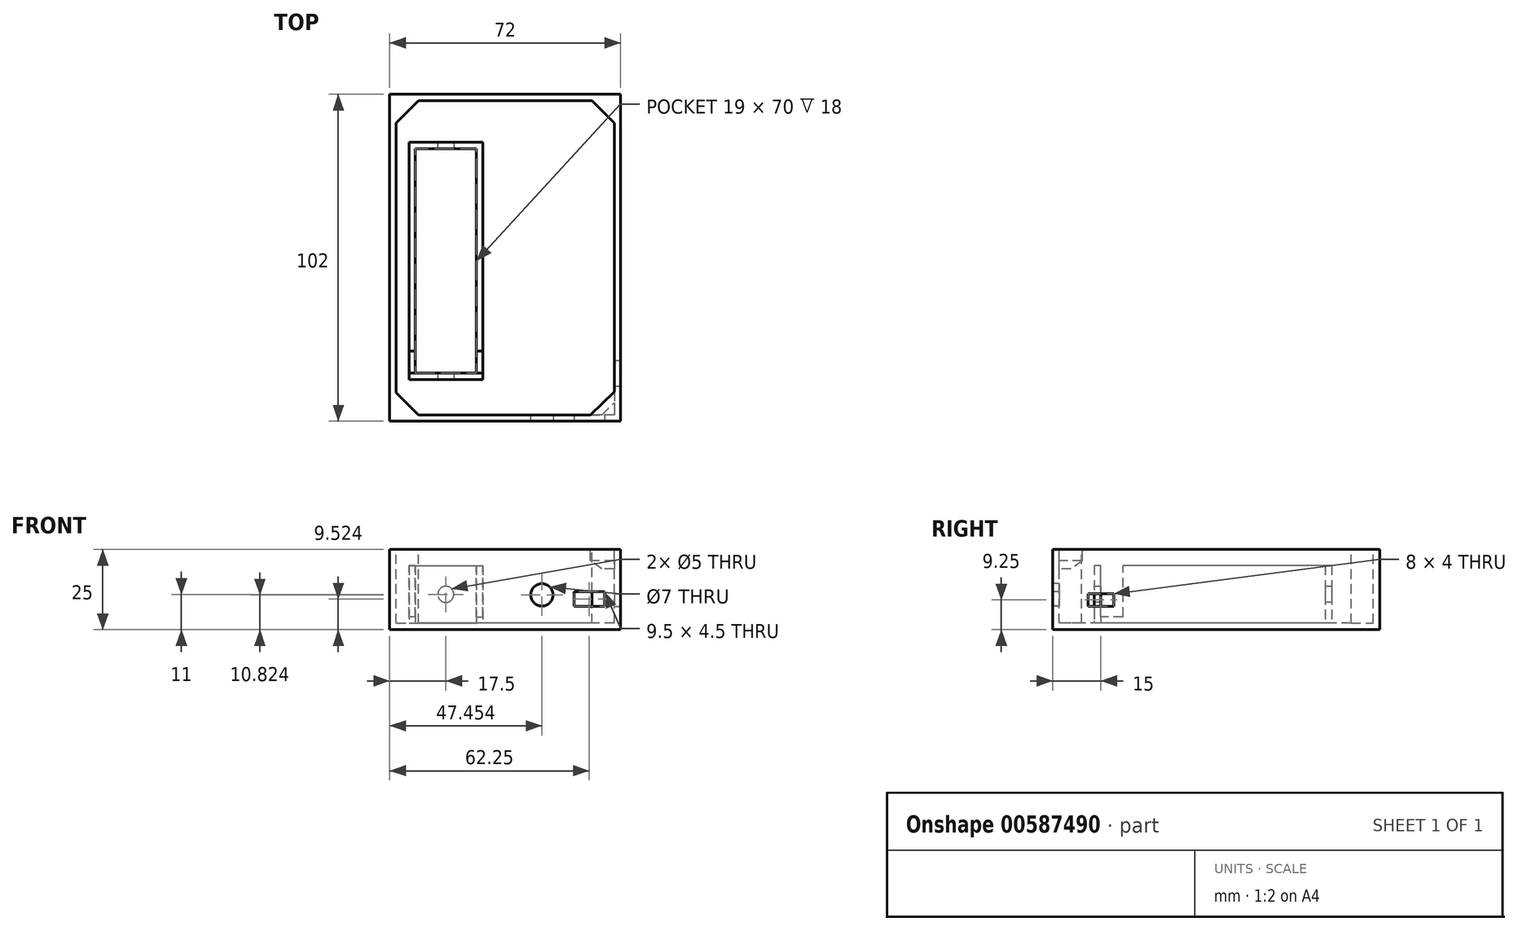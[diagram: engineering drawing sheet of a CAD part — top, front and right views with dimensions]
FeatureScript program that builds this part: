
annotation { "Feature Type Name" : "Feature", "Feature Type Description" : "" }
export const myFeature = defineFeature(function(context is Context, id is Id, definition is map)
    precondition{}
    {
        {
            var Q0;
            Q0=qCreatedBy(makeId("Top.planeOp"),FACE);
            var sketch = newSketch(context, id + "F0", { "sketchPlane" : qUnion([Q0])});
            skLineSegment(sketch, "E0.bottom", {"start": v(36, 51) * mm, "end": v(-36, 51) * mm});
            skLineSegment(sketch, "E0.top", {"start": v(36, -51) * mm, "end": v(-36, -51) * mm});
            skLineSegment(sketch, "E0.left", {"start": v(36, 51) * mm, "end": v(36, -51) * mm});
            skLineSegment(sketch, "E0.right", {"start": v(-36, 51) * mm, "end": v(-36, -51) * mm});
            skPoint(sketch, "E0.middle", {"position": v(0, 0) * mm});
            skSolve(sketch);
        }
        {
            var Q0;
            Q0 = qSketchRegion(id + "F0", true);
            extrude(context, id + "F1", {"entities" : qUnion([Q0]), "depth" : 25 * mm, "offsetDistance" : 25 * mm});
        }
        {
            var Q0;
            Q0=makeQuery(id+"F1.opExtrude","CAP_FACE",FACE,{"disambiguationData":[OSD([sQuery(id+"F0.wireOp",EDGE,"E0.bottom"),sQuery(id+"F0.wireOp",EDGE,"E0.top"),sQuery(id+"F0.wireOp",EDGE,"E0.left"),sQuery(id+"F0.wireOp",EDGE,"E0.right")])],"isStart":false});
            var sketch = newSketch(context, id + "F2", { "sketchPlane" : qUnion([Q0])});
            skLineSegment(sketch, "E1.bottom", {"start": v(27.06, 49) * mm, "end": v(-27.06, 49) * mm});
            skLineSegment(sketch, "E1.top", {"start": v(34, -49) * mm, "end": v(-27.06, -49) * mm});
            skLineSegment(sketch, "E1.left", {"start": v(34, 42.06) * mm, "end": v(34, -49) * mm});
            skLineSegment(sketch, "E1.right", {"start": v(-34, 42.06) * mm, "end": v(-34, -42.06) * mm});
            skPoint(sketch, "E1.middle", {"position": v(0, 0) * mm});
            skLineSegment(sketch, "E2", {"start": v(-34, 42.06) * mm, "end": v(-27.06, 49) * mm});
            skLineSegment(sketch, "E3.MirrorCS", {"start": v(34, 42.06) * mm, "end": v(27.06, 49) * mm});
            skLineSegment(sketch, "E4.MirrorCS", {"start": v(-34, -42.06) * mm, "end": v(-27.06, -49) * mm});
            skPoint(sketch, "E5.orphan", {"position": v(-34, 49) * mm});
            skPoint(sketch, "E6.orphan", {"position": v(34, 49) * mm});
            skPoint(sketch, "E7.orphan", {"position": v(-34, -49) * mm});
            skSolve(sketch);
        }
        {
            var Q0;
            Q0 = qSketchRegion(id + "F2", true);
            extrude(context, id + "F3", {"entities" : qUnion([Q0]), "operationType" : NewBodyOperationType.REMOVE, "oppositeDirection" : true, "depth" : 23 * mm, "offsetDistance" : 25 * mm});
        }
        {
            var Q0;
            Q0=makeQuery(id+"F1.opExtrude","SWEPT_FACE",FACE,{"disambiguationData":[OSD([sQuery(id+"F0.wireOp",EDGE,"E0.top")])]});
            var sketch = newSketch(context, id + "F4", { "sketchPlane" : qUnion([Q0])});
            skLineSegment(sketch, "E8", {"start": v(-36, 7.27) * mm, "end": v(36, 7.27) * mm, "construction": true});
            skLineSegment(sketch, "E9.bottom", {"start": v(31, 7.27) * mm, "end": v(21.5, 7.27) * mm});
            skLineSegment(sketch, "E9.top", {"start": v(31, 11.77) * mm, "end": v(21.5, 11.77) * mm});
            skLineSegment(sketch, "E9.left", {"start": v(31, 7.27) * mm, "end": v(31, 11.77) * mm});
            skLineSegment(sketch, "E9.right", {"start": v(21.5, 7.27) * mm, "end": v(21.5, 11.77) * mm});
            skCircle(sketch, "E10", {"center": v(11.45, 10.82) * mm, "radius": 3.5 * mm});
            skSolve(sketch);
        }
        {
            var Q0;
            Q0 = qSketchRegion(id + "F4", true);
            extrude(context, id + "F5", {"entities" : qUnion([Q0]), "operationType" : NewBodyOperationType.REMOVE, "oppositeDirection" : true, "depth" : 3 * mm, "offsetDistance" : 25 * mm});
        }
        {
            var Q0;
            Q0 = qSketchRegion(id + "F4", true);
            extrude(context, id + "F6", {"entities" : qUnion([Q0]), "operationType" : NewBodyOperationType.REMOVE, "oppositeDirection" : true, "depth" : 3 * mm, "offsetDistance" : 25 * mm});
        }
        {
            var Q0;
            Q0=makeQuery(id+"F1.opExtrude","SWEPT_FACE",FACE,{"disambiguationData":[OSD([sQuery(id+"F0.wireOp",EDGE,"E0.left")])]});
            var sketch = newSketch(context, id + "F7", { "sketchPlane" : qUnion([Q0])});
            skLineSegment(sketch, "E11", {"start": v(-51, 7.25) * mm, "end": v(51, 7.25) * mm, "construction": true});
            skLineSegment(sketch, "E12.bottom", {"start": v(-40, 7.25) * mm, "end": v(-32, 7.25) * mm});
            skLineSegment(sketch, "E12.top", {"start": v(-40, 11.25) * mm, "end": v(-32, 11.25) * mm});
            skLineSegment(sketch, "E12.left", {"start": v(-40, 7.25) * mm, "end": v(-40, 11.25) * mm});
            skLineSegment(sketch, "E12.right", {"start": v(-32, 7.25) * mm, "end": v(-32, 11.25) * mm});
            skSolve(sketch);
        }
        {
            var Q0;
            Q0 = qSketchRegion(id + "F7", true);
            extrude(context, id + "F8", {"entities" : qUnion([Q0]), "operationType" : NewBodyOperationType.REMOVE, "oppositeDirection" : true, "depth" : 3 * mm, "offsetDistance" : 25 * mm});
        }
        {
            var Q0;
            Q0=makeQuery(id+"F3.boolean.opBoolean","COPY",FACE,{"derivedFrom":makeQuery(id+"F3.opExtrude","CAP_FACE",FACE,{"disambiguationData":[OSD([sQuery(id+"F2.wireOp",EDGE,"E1.bottom"),sQuery(id+"F2.wireOp",EDGE,"E1.top"),sQuery(id+"F2.wireOp",EDGE,"E1.left"),sQuery(id+"F2.wireOp",EDGE,"E1.right"),sQuery(id+"F2.wireOp",EDGE,"E2"),sQuery(id+"F2.wireOp",EDGE,"E3.MirrorCS"),sQuery(id+"F2.wireOp",EDGE,"E4.MirrorCS")])],"isStart":false})});
            var sketch = newSketch(context, id + "F9", { "sketchPlane" : qUnion([Q0])});
            skSolve(sketch);
        }
        {
            var Q0;
            Q0=makeQuery(id+"F9.imprint","IMPRINT",FACE,{"disambiguationData":[TD([[makeQuery(id+"F9.imprint","IMPRINT",EDGE,{"derivedFrom":makeQuery(id+"F3.boolean.opBoolean","COPY",EDGE,{"derivedFrom":makeQuery(id+"F3.opExtrude","CAP_EDGE",EDGE,{"disambiguationData":[OSD([sQuery(id+"F2.wireOp",EDGE,"E1.bottom")])],"isStart":false})})}),1.0]])]});
            var sketch = newSketch(context, id + "F10", { "sketchPlane" : qUnion([Q0])});
            skLineSegment(sketch, "E13.bottom", {"start": v(-28, 34) * mm, "end": v(-9, 34) * mm});
            skLineSegment(sketch, "E13.top", {"start": v(-28, -36) * mm, "end": v(-9, -36) * mm});
            skLineSegment(sketch, "E13.left", {"start": v(-28, 34) * mm, "end": v(-28, -36) * mm});
            skLineSegment(sketch, "E13.right", {"start": v(-9, 34) * mm, "end": v(-9, -36) * mm});
            skLineSegment(sketch, "E14.0", {"start": v(-30, 36) * mm, "end": v(-7, 36) * mm});
            skLineSegment(sketch, "E14.1", {"start": v(-30, 36) * mm, "end": v(-30, -38) * mm});
            skLineSegment(sketch, "E14.2", {"start": v(-30, -38) * mm, "end": v(-7, -38) * mm});
            skLineSegment(sketch, "E14.3", {"start": v(-7, 36) * mm, "end": v(-7, -38) * mm});
            skSolve(sketch);
        }
        {
            var Q0;
            Q0 = qSketchRegion(id + "F10", true);
            extrude(context, id + "F11", {"entities" : qUnion([Q0]), "operationType" : NewBodyOperationType.ADD, "depth" : 18 * mm, "offsetDistance" : 25 * mm});
        }
        {
            var Q0;
            Q0=makeQuery(id+"F11.opExtrude","CAP_FACE",FACE,{"disambiguationData":[OSD([sQuery(id+"F10.wireOp",EDGE,"E13.bottom"),sQuery(id+"F10.wireOp",EDGE,"E13.top"),sQuery(id+"F10.wireOp",EDGE,"E13.left"),sQuery(id+"F10.wireOp",EDGE,"E13.right"),sQuery(id+"F10.wireOp",EDGE,"E14.0"),sQuery(id+"F10.wireOp",EDGE,"E14.1"),sQuery(id+"F10.wireOp",EDGE,"E14.2"),sQuery(id+"F10.wireOp",EDGE,"E14.3")])],"isStart":false});
            var sketch = newSketch(context, id + "F12", { "sketchPlane" : qUnion([Q0])});
            skLineSegment(sketch, "E15", {"start": v(-18.5, -36) * mm, "end": v(-18.5, 40.4) * mm, "construction": true});
            skLineSegment(sketch, "E16.bottom", {"start": v(-28, -36) * mm, "end": v(-30, -36) * mm});
            skLineSegment(sketch, "E16.top", {"start": v(-28, -29.06) * mm, "end": v(-30, -29.06) * mm});
            skLineSegment(sketch, "E16.left", {"start": v(-28, -36) * mm, "end": v(-28, -29.06) * mm});
            skLineSegment(sketch, "E16.right", {"start": v(-30, -36) * mm, "end": v(-30, -29.06) * mm});
            skLineSegment(sketch, "E17.MirrorCS", {"start": v(-7, -36) * mm, "end": v(-7, -29.06) * mm});
            skLineSegment(sketch, "E18.MirrorCS", {"start": v(-9, -36) * mm, "end": v(-9, -29.06) * mm});
            skLineSegment(sketch, "E19.MirrorCS", {"start": v(-9, -36) * mm, "end": v(-7, -36) * mm});
            skLineSegment(sketch, "E20.MirrorCS", {"start": v(-9, -29.06) * mm, "end": v(-7, -29.06) * mm});
            skSolve(sketch);
        }
        {
            var Q0;
            Q0 = qSketchRegion(id + "F12", true);
            extrude(context, id + "F13", {"entities" : qUnion([Q0]), "operationType" : NewBodyOperationType.REMOVE, "oppositeDirection" : true, "depth" : 16 * mm, "offsetDistance" : 25 * mm});
        }
        {
            var Q0;
            Q0=makeQuery(id+"F11.opExtrude","SWEPT_FACE",FACE,{"disambiguationData":[OSD([sQuery(id+"F10.wireOp",EDGE,"E14.2")])]});
            var sketch = newSketch(context, id + "F14", { "sketchPlane" : qUnion([Q0])});
            skCircle(sketch, "E21", {"center": v(-18.5, 11) * mm, "radius": 2.5 * mm});
            skSolve(sketch);
        }
        {
            var Q0;
            Q0 = qSketchRegion(id + "F14", true);
            extrude(context, id + "F15", {"entities" : qUnion([Q0]), "operationType" : NewBodyOperationType.REMOVE, "oppositeDirection" : true, "depth" : 75 * mm, "offsetDistance" : 25 * mm});
        }
        {
            var Q0;
            Q0=makeQuery(id+"F1.opExtrude","CAP_FACE",FACE,{"disambiguationData":[OSD([sQuery(id+"F0.wireOp",EDGE,"E0.bottom"),sQuery(id+"F0.wireOp",EDGE,"E0.top"),sQuery(id+"F0.wireOp",EDGE,"E0.left"),sQuery(id+"F0.wireOp",EDGE,"E0.right")])],"isStart":false});
            var sketch = newSketch(context, id + "F16", { "sketchPlane" : qUnion([Q0])});
            skLineSegment(sketch, "E22", {"start": v(26.53, -49) * mm, "end": v(34, -41.77) * mm});
            skLineSegment(sketch, "E23", {"start": v(34, -41.77) * mm, "end": v(34, -49) * mm});
            skLineSegment(sketch, "E24", {"start": v(34, -49) * mm, "end": v(26.53, -49) * mm});
            skSolve(sketch);
        }
        {
            var Q0;
            Q0 = qSketchRegion(id + "F16", true);
            extrude(context, id + "F17", {"entities" : qUnion([Q0]), "operationType" : NewBodyOperationType.ADD, "depth" : -6 * mm, "offsetDistance" : 25 * mm});
        }
        {
            var Q0;
            Q0=makeQuery(id+"F17.opExtrude","CAP_EDGE",EDGE,{"disambiguationData":[OSD([sQuery(id+"F16.wireOp",EDGE,"E22")])],"isStart":false});
            chamfer(context, id + "F18", {"entities" : qUnion([Q0]), "width" : 2.5 * mm, "tangentPropagation" : true});
        }
    });
